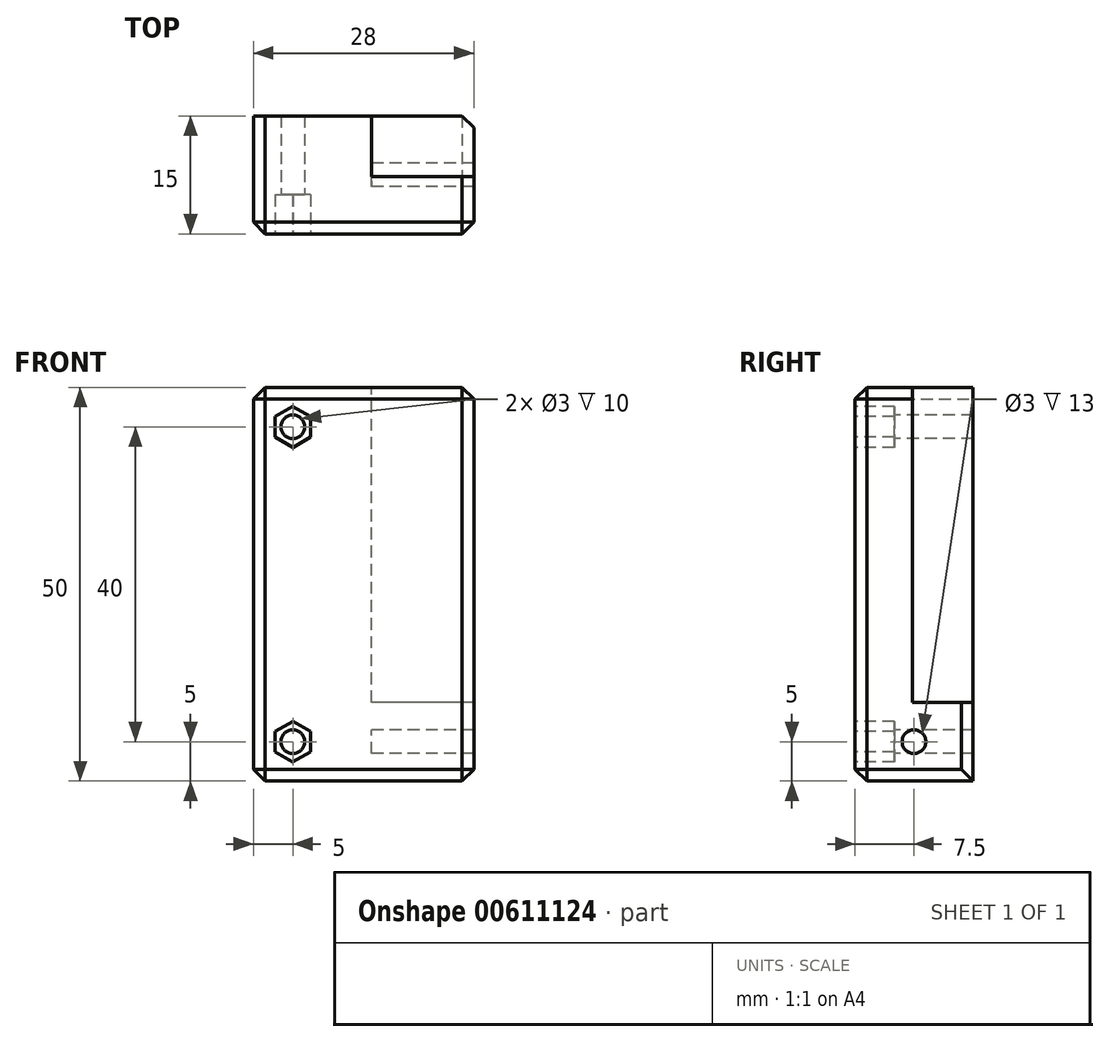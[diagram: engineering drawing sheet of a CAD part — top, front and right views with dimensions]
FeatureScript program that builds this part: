
annotation { "Feature Type Name" : "Feature", "Feature Type Description" : "" }
export const myFeature = defineFeature(function(context is Context, id is Id, definition is map)
    precondition{}
    {
        {
            var Q0;
            Q0=qCreatedBy(makeId("Right.planeOp"),FACE);
            var sketch = newSketch(context, id + "F0", { "sketchPlane" : qUnion([Q0])});
            skLineSegment(sketch, "E0.bottom", {"start": v(0, 0) * mm, "end": v(15, 0) * mm});
            skLineSegment(sketch, "E0.top", {"start": v(0, 50) * mm, "end": v(15, 50) * mm});
            skLineSegment(sketch, "E0.left", {"start": v(0, 0) * mm, "end": v(0, 50) * mm});
            skLineSegment(sketch, "E0.right", {"start": v(15, 0) * mm, "end": v(15, 50) * mm});
            skLineSegment(sketch, "E1.bottom", {"start": v(15, 50) * mm, "end": v(7.3, 50) * mm});
            skLineSegment(sketch, "E1.top", {"start": v(15, 10) * mm, "end": v(7.3, 10) * mm});
            skLineSegment(sketch, "E1.left", {"start": v(15, 50) * mm, "end": v(15, 10) * mm});
            skLineSegment(sketch, "E1.right", {"start": v(7.3, 50) * mm, "end": v(7.3, 10) * mm});
            skCircle(sketch, "E2", {"center": v(7.5, 5) * mm, "radius": 1.5 * mm});
            skSolve(sketch);
        }
        {
            var Q0;
            Q0=makeQuery(id+"F0.imprint","IMPRINT",FACE,{"disambiguationData":[TD([[makeQuery(id+"F0.imprint","IMPRINT",EDGE,{"derivedFrom":sQuery(id+"F0.wireOp",EDGE,"E0.bottom")}),1.0]])]});
            extrude(context, id + "F1", {"entities" : qUnion([Q0]), "depth" : 13 * mm, "offsetDistance" : 25 * mm});
        }
        {
            var Q0;
            Q0 = qSketchRegion(id + "F0", true);
            var Q1;
            Q1=makeQuery(id+"F0.imprint","IMPRINT",FACE,{"disambiguationData":[TD([[makeQuery(id+"F0.imprint","IMPRINT",EDGE,{"derivedFrom":sQuery(id+"F0.wireOp",EDGE,"E2")}),1.0]])]});
            extrude(context, id + "F2", {"entities" : qUnion([Q0, Q1]), "operationType" : NewBodyOperationType.ADD, "oppositeDirection" : true, "depth" : 15 * mm, "offsetDistance" : 25 * mm});
        }
        {
            var Q0;
            {var subQ0=sQuery(id+"F0.wireOp",EDGE,"E0.left");Q0=makeQuery(id+"F2.boolean.opBoolean","MERGE",FACE,{"derivedFrom":[makeQuery(id+"F1.opExtrude","SWEPT_FACE",FACE,{"disambiguationData":[OSD([subQ0])]}),makeQuery(id+"F2.opExtrude","SWEPT_FACE",FACE,{"disambiguationData":[OSD([subQ0])]})]});}
            var sketch = newSketch(context, id + "F3", { "sketchPlane" : qUnion([Q0])});
            skCircle(sketch, "E3", {"center": v(-10, 5) * mm, "radius": 1.5 * mm});
            skCircle(sketch, "E4.cCircle", {"center": v(-10, 5) * mm, "radius": 2.25 * mm, "construction": true});
            skLineSegment(sketch, "E4.0", {"start": v(-7.76, 3.7) * mm, "end": v(-10.01, 2.4) * mm});
            skLineSegment(sketch, "E4.1", {"start": v(-10.01, 2.4) * mm, "end": v(-12.26, 3.71) * mm});
            skLineSegment(sketch, "E4.2", {"start": v(-12.26, 3.71) * mm, "end": v(-12.24, 6.3) * mm});
            skLineSegment(sketch, "E4.3", {"start": v(-12.24, 6.3) * mm, "end": v(-9.99, 7.6) * mm});
            skLineSegment(sketch, "E4.4", {"start": v(-9.99, 7.6) * mm, "end": v(-7.74, 6.29) * mm});
            skLineSegment(sketch, "E4.5", {"start": v(-7.74, 6.29) * mm, "end": v(-7.76, 3.7) * mm});
            skPoint(sketch, "E4.0.midPoint", {"position": v(-8.88, 3.05) * mm});
            skCircle(sketch, "E5", {"center": v(-10, 45) * mm, "radius": 1.5 * mm});
            skCircle(sketch, "E6.cCircle", {"center": v(-10, 45) * mm, "radius": 2.25 * mm, "construction": true});
            skLineSegment(sketch, "E6.0", {"start": v(-10.02, 47.6) * mm, "end": v(-7.76, 46.31) * mm});
            skLineSegment(sketch, "E6.1", {"start": v(-7.76, 46.31) * mm, "end": v(-7.74, 43.71) * mm});
            skLineSegment(sketch, "E6.2", {"start": v(-7.74, 43.71) * mm, "end": v(-9.98, 42.4) * mm});
            skLineSegment(sketch, "E6.3", {"start": v(-9.98, 42.4) * mm, "end": v(-12.24, 43.69) * mm});
            skLineSegment(sketch, "E6.4", {"start": v(-12.24, 43.69) * mm, "end": v(-12.26, 46.29) * mm});
            skLineSegment(sketch, "E6.5", {"start": v(-12.26, 46.29) * mm, "end": v(-10.02, 47.6) * mm});
            skPoint(sketch, "E6.0.midPoint", {"position": v(-8.89, 46.96) * mm});
            skSolve(sketch);
        }
        {
            var Q0;
            Q0=makeQuery(id+"F3.imprint","IMPRINT",FACE,{"disambiguationData":[TD([[makeQuery(id+"F3.imprint","IMPRINT",EDGE,{"derivedFrom":sQuery(id+"F3.wireOp",EDGE,"E5")}),1.0]])]});
            var Q1;
            Q1=makeQuery(id+"F3.imprint","IMPRINT",FACE,{"disambiguationData":[TD([[makeQuery(id+"F3.imprint","IMPRINT",EDGE,{"derivedFrom":sQuery(id+"F3.wireOp",EDGE,"E3")}),1.0]])]});
            extrude(context, id + "F4", {"entities" : qUnion([Q0, Q1]), "operationType" : NewBodyOperationType.REMOVE, "endBound" : BoundingType.THROUGH_ALL, "oppositeDirection" : true, "depth" : 25 * mm, "offsetDistance" : 25 * mm});
        }
        {
            var Q0;
            Q0 = qSketchRegion(id + "F3", true);
            extrude(context, id + "F5", {"entities" : qUnion([Q0]), "operationType" : NewBodyOperationType.REMOVE, "endBound" : BoundingType.SYMMETRIC, "oppositeDirection" : true, "depth" : 10 * mm, "offsetDistance" : 25 * mm});
        }
        {
            var Q0;
            Q0=makeQuery(id+"F2.opExtrude","CAP_EDGE",EDGE,{"disambiguationData":[OSD([sQuery(id+"F0.wireOp",EDGE,"E0.left")])],"isStart":false});
            var Q1;
            {var subQ0=sQuery(id+"F0.wireOp",EDGE,"E0.left");var subQ1=sQuery(id+"F0.wireOp",EDGE,"E0.top");Q1=makeQuery(id+"F2.boolean.opBoolean","MERGE",EDGE,{"derivedFrom":[makeQuery(id+"F1.opExtrude","SWEPT_EDGE",EDGE,{"disambiguationData":[OSD([subQ1,subQ0])]}),makeQuery(id+"F2.opExtrude","SWEPT_EDGE",EDGE,{"disambiguationData":[OSD([subQ1,subQ0])]})]});}
            var Q2;
            Q2=makeQuery(id+"F1.opExtrude","CAP_EDGE",EDGE,{"disambiguationData":[OSD([sQuery(id+"F0.wireOp",EDGE,"E0.left")])],"isStart":false});
            var Q3;
            Q3=makeQuery(id+"F2.opExtrude","CAP_EDGE",EDGE,{"disambiguationData":[OSD([sQuery(id+"F0.wireOp",EDGE,"E0.top"),sQuery(id+"F0.wireOp",EDGE,"E1.bottom")])],"isStart":false});
            var Q4;
            Q4=makeQuery(id+"F2.opExtrude","CAP_EDGE",EDGE,{"disambiguationData":[OSD([sQuery(id+"F0.wireOp",EDGE,"E0.bottom")])],"isStart":false});
            var Q5;
            {var subQ0=sQuery(id+"F0.wireOp",EDGE,"E0.left");var subQ1=sQuery(id+"F0.wireOp",EDGE,"E0.bottom");Q5=makeQuery(id+"F2.boolean.opBoolean","MERGE",EDGE,{"derivedFrom":[makeQuery(id+"F1.opExtrude","SWEPT_EDGE",EDGE,{"disambiguationData":[OSD([subQ1,subQ0])]}),makeQuery(id+"F2.opExtrude","SWEPT_EDGE",EDGE,{"disambiguationData":[OSD([subQ1,subQ0])]})]});}
            var Q6;
            Q6=makeQuery(id+"F1.opExtrude","CAP_EDGE",EDGE,{"disambiguationData":[OSD([sQuery(id+"F0.wireOp",EDGE,"E0.bottom")])],"isStart":false});
            var Q7;
            Q7=makeQuery(id+"F1.opExtrude","CAP_EDGE",EDGE,{"disambiguationData":[OSD([sQuery(id+"F0.wireOp",EDGE,"E0.top")])],"isStart":false});
            var Q8;
            Q8=makeQuery(id+"F1.opExtrude","CAP_EDGE",EDGE,{"disambiguationData":[OSD([sQuery(id+"F0.wireOp",EDGE,"E0.right")])],"isStart":false});
            chamfer(context, id + "F6", {"entities" : qUnion([Q0, Q1, Q2, Q3, Q4, Q5, Q6, Q7, Q8]), "width" : 1.5 * mm, "tangentPropagation" : true});
        }
    });
